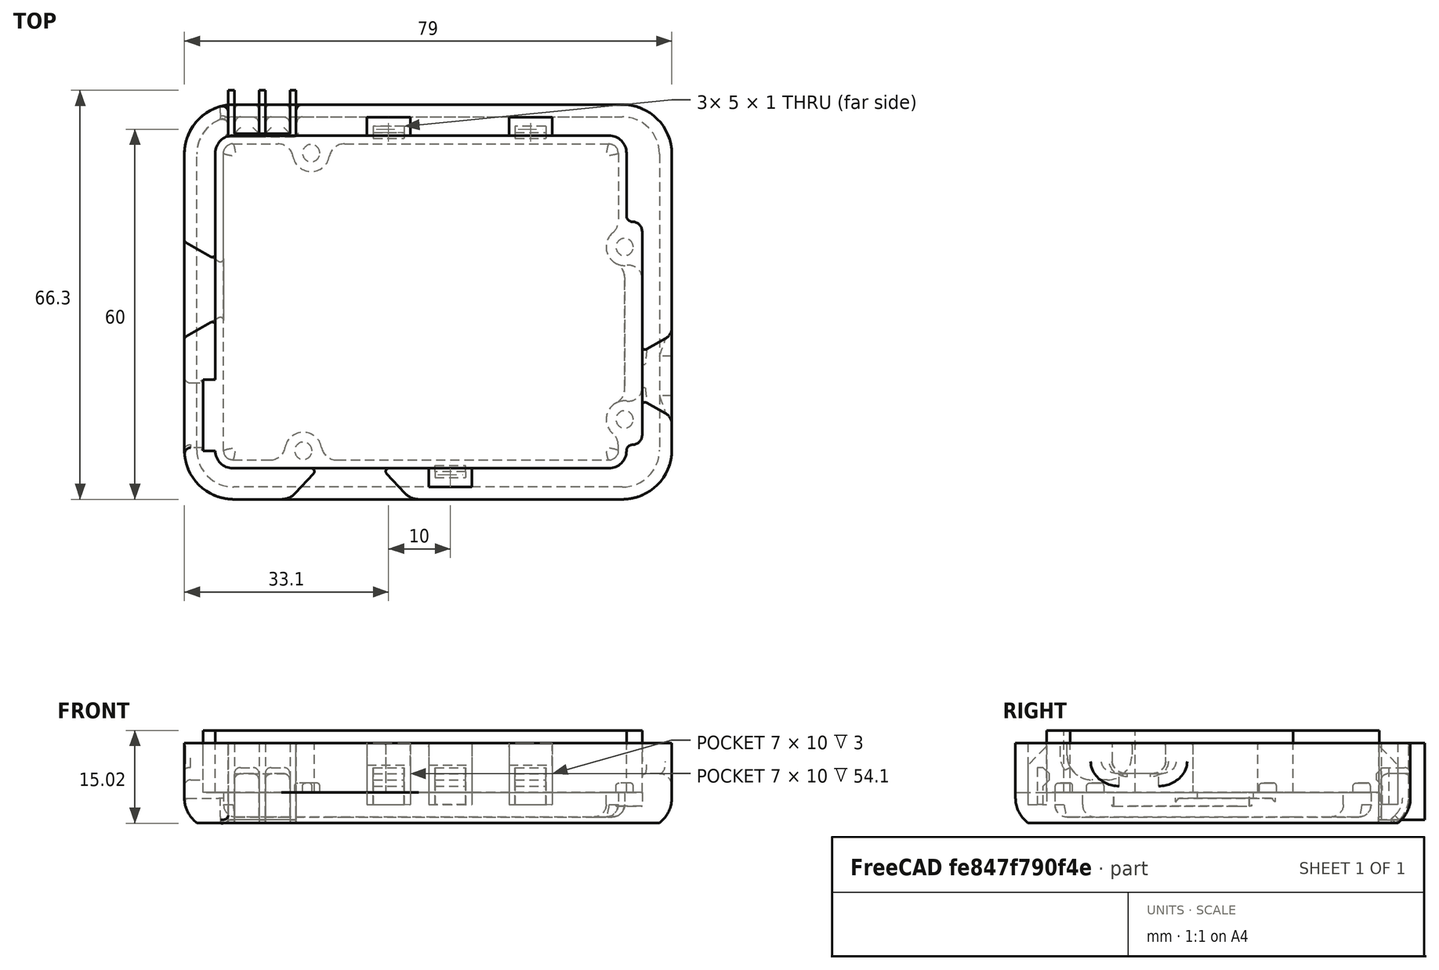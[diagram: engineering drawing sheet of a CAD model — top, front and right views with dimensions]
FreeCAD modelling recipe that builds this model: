
FCSTD DOCUMENT  (FreeCAD 0.16R6712 (Git))
Label: base_alhambra
License: All rights reserved
LicenseURL: http://en.wikipedia.org/wiki/All_rights_reserved
objects: PartDesign::Fillet×18, Sketcher::SketchObject×15, PartDesign::Pocket×9, PartDesign::Pad×6, Part::MultiFuse×5, Part::Cylinder×4, Part::Box×3, Part::Cut×1, PartDesign::Chamfer×1, Mesh::Feature×1, Part::Feature×1, Part::FeaturePython×1, Part::Mirroring×1
note: 80 computed .brp shape members not serialized (recipe doc carries the construction recipe); baked Part::Feature solids carry a one-line shape summary decoded from their .brp

FEATURE [Part::Cylinder] Cylinder  label="Cilindro"
  Angle = 360
  Height = 4.5
  Placement = pos=(-20.32,-24.13,0) rot=(0,0,1;0rad)
  Radius = 1.4
FEATURE [Part::Cylinder] Cylinder001  label="Cilindro001"
  Angle = 360
  Height = 4.5
  Placement = pos=(31.75,-19.05,0) rot=(0,0,1;0rad)
  Radius = 1.4
FEATURE [Part::Cylinder] Cylinder002  label="Cilindro002"
  Angle = 360
  Height = 4.5
  Placement = pos=(31.75,8.9,0) rot=(0,0,1;0rad)
  Radius = 1.4
FEATURE [Part::Cylinder] Cylinder003  label="Cilindro003"
  Angle = 360
  Height = 4.5
  Placement = pos=(-19.05,24.13,0) rot=(0,0,1;0rad)
  Radius = 1.4
FEATURE [Sketcher::SketchObject] Sketch
  Placement = pos=(0,0,3) rot=(0,0,1;0rad)
  sketch-geometry (16):
    g0: LineSegment StartX=-34.59 StartY=-24.13 StartZ=0 EndX=-36.59 EndY=-24.13 EndZ=0
    g1: LineSegment StartX=-36.59 StartY=-24.13 StartZ=0 EndX=-36.59 EndY=-12.63 EndZ=0
    g2: LineSegment StartX=-36.59 StartY=-12.63 StartZ=0 EndX=-34.59 EndY=-12.63 EndZ=0
    g3: LineSegment StartX=-34.59 StartY=-12.63 StartZ=0 EndX=-34.59 EndY=24.13 EndZ=0
    g4: ArcOfCircle CenterX=-31.75 CenterY=24.13 CenterZ=0 NormalX=0 NormalY=0 NormalZ=1 Radius=2.84 StartAngle=1.5708 EndAngle=3.14159
    g5: LineSegment StartX=-31.75 StartY=26.97 StartZ=0 EndX=29.21 EndY=26.97 EndZ=0
    g6: ArcOfCircle CenterX=29.21 CenterY=24.13 CenterZ=0 NormalX=0 NormalY=0 NormalZ=1 Radius=2.84 StartAngle=3.7035e-08 EndAngle=1.5708
    g7: LineSegment StartX=32.05 StartY=24.13 StartZ=0 EndX=32.05 EndY=13.97 EndZ=0
    g8: ArcOfCircle CenterX=33.02 CenterY=13.97 CenterZ=0 NormalX=0 NormalY=0 NormalZ=1 Radius=0.969997 StartAngle=3.14159 EndAngle=4.71239
    g9: ArcOfCircle CenterX=33.02 CenterY=11.43 CenterZ=0 NormalX=0 NormalY=0 NormalZ=1 Radius=1.57 StartAngle=6.28319 EndAngle=7.85398
    g10: LineSegment StartX=34.59 StartY=11.43 StartZ=0 EndX=34.59 EndY=-21.59 EndZ=0
    g11: ArcOfCircle CenterX=33.02 CenterY=-21.59 CenterZ=0 NormalX=0 NormalY=0 NormalZ=1 Radius=1.57 StartAngle=4.71239 EndAngle=6.28319
    g12: ArcOfCircle CenterX=33.02 CenterY=-24.13 CenterZ=0 NormalX=0 NormalY=0 NormalZ=1 Radius=0.97 StartAngle=1.5708 EndAngle=3.1416
    g13: ArcOfCircle CenterX=29.21 CenterY=-24.13 CenterZ=0 NormalX=0 NormalY=0 NormalZ=1 Radius=2.83999 StartAngle=4.71238 EndAngle=6.28319
    g14: LineSegment StartX=29.21 StartY=-26.97 StartZ=0 EndX=-31.75 EndY=-26.97 EndZ=0
    g15: ArcOfCircle CenterX=-31.75 CenterY=-24.13 CenterZ=0 NormalX=0 NormalY=0 NormalZ=1 Radius=2.84 StartAngle=3.14159 EndAngle=4.71239
  constraints (56):
    c: Horizontal(g0)
    c: Coincident(g0,g1)
    c: Vertical(g1)
    c: Coincident(g1,g2)
    c: Horizontal(g2)
    c: Coincident(g2,g3)
    c: Vertical(g3)
    c: Coincident(g4,g3)
    c: DistanceY(g2,g-1) = 12.63
    c: DistanceX(g2,g-1) = 34.59
    c: DistanceY(g-1,g3) = 24.13
    c: Tangent(g3,g4)
    c: DistanceY(g-1,g4) = 26.97
    c: DistanceX(g2,g2) = 2
    c: DistanceY(g1,g1) = 11.5
    c: DistanceX(g0,g0) = 2
    c: Coincident(g5,g4)
    c: Horizontal(g5)
    c: DistanceX(g5,g5) = 60.96
    c: Tangent(g4,g5)
    c: Coincident(g6,g5)
    c: Tangent(g6,g5)
    c: DistanceY(g-1,g6) = 24.13
    c: Coincident(g7,g6)
    c: Vertical(g7)
    c: DistanceY(g7,g7) = 10.16
    c: Tangent(g7,g6)
    c: Coincident(g8,g7)
    c: Coincident(g9,g8)
    c: Tangent(g8,g9)
    c: Tangent(g8,g7)
    c: Coincident(g10,g9)
    c: Vertical(g10)
    c: DistanceX(g-1,g10) = 34.59
    c: DistanceY(g10,g-1) = 21.59
    c: Tangent(g10,g9)
    c: DistanceY(g-1,g9) = 11.43
    c: Coincident(g11,g10)
    c: Coincident(g12,g11)
    c: Coincident(g13,g12)
    c: Tangent(g11,g12)
    c: Tangent(g11,g10)
    c: Tangent(g13,g12)
    c: DistanceX(g7,g8) = 0.97
    c: DistanceX(g11,g10) = 1.57
    c: DistanceX(g12,g11) = 0.97
    c: Radius(g11) = 1.57
    c: DistanceY(g13,g-1) = 26.97
    c: Coincident(g14,g13)
    c: Horizontal(g14)
    c: DistanceX(g14,g-1) = 31.75
    c: Coincident(g15,g14)
    c: Coincident(g15,g0)
    c: Radius(g15) = 2.84
    c: DistanceX(g-1,g13) = 29.21
    c: Tangent(g14,g13)
FEATURE [PartDesign::Pad] Pad  label="placa"
  Length = 10
  Length2 = 100
  Placement = pos=(0,0,3) rot=(0,0,1;0rad)
  Sketch = -> Sketch
  Type = 0
FEATURE [Sketcher::SketchObject] Sketch001
  ExternalGeometry = -> [Pad]
  Placement = pos=(0,0,3) rot=(1,0,0;3.14159rad)
  Support = -> Pad [Face17]
  sketch-geometry (24):
    g0: ArcOfCircle CenterX=29.21 CenterY=24.13 CenterZ=0 NormalX=0 NormalY=0 NormalZ=1 Radius=1.5 StartAngle=6.28318 EndAngle=7.85398
    g1: ArcOfCircle CenterX=31.77 CenterY=19.04 CenterZ=0 NormalX=0 NormalY=0 NormalZ=1 Radius=3 StartAngle=2.27479 EndAngle=4.23644
    g2: ArcOfCircle CenterX=-20.32 CenterY=24.13 CenterZ=0 NormalX=0 NormalY=0 NormalZ=1 Radius=3 StartAngle=3.32443 EndAngle=6.10035
    g3: ArcOfCircle CenterX=-14.9117 CenterY=23.13 CenterZ=0 NormalX=0 NormalY=0 NormalZ=1 Radius=2.5 StartAngle=1.5708 EndAngle=2.95876
    g4: LineSegment StartX=-14.9117 StartY=25.63 StartZ=0 EndX=29.21 EndY=25.63 EndZ=0
    g5: ArcOfCircle CenterX=-31.75 CenterY=24.13 CenterZ=0 NormalX=0 NormalY=0 NormalZ=1 Radius=1.50001 StartAngle=1.5708 EndAngle=3.14159
    g6: LineSegment StartX=-31.75 StartY=25.63 StartZ=0 EndX=-25.7283 EndY=25.63 EndZ=0
    g7: ArcOfCircle CenterX=-25.7283 CenterY=23.13 CenterZ=0 NormalX=0 NormalY=0 NormalZ=1 Radius=2.5 StartAngle=0.182833 EndAngle=1.5708
    g8: LineSegment StartX=-33.25 StartY=24.13 StartZ=0 EndX=-33.25 EndY=-24.13 EndZ=0
    g9: ArcOfCircle CenterX=-31.75 CenterY=-24.13 CenterZ=0 NormalX=0 NormalY=0 NormalZ=1 Radius=1.50001 StartAngle=3.14159 EndAngle=4.71239
    g10: ArcOfCircle CenterX=-19.05 CenterY=-24.13 CenterZ=0 NormalX=0 NormalY=0 NormalZ=1 Radius=3 StartAngle=0.182835 EndAngle=2.95876
    g11: ArcOfCircle CenterX=-24.4583 CenterY=-23.13 CenterZ=0 NormalX=0 NormalY=0 NormalZ=1 Radius=2.5 StartAngle=4.71239 EndAngle=6.10035
    g12: LineSegment StartX=-31.75 StartY=-25.63 StartZ=0 EndX=-24.4583 EndY=-25.63 EndZ=0
    g13: ArcOfCircle CenterX=-13.6417 CenterY=-23.13 CenterZ=0 NormalX=0 NormalY=0 NormalZ=1 Radius=2.5 StartAngle=3.32443 EndAngle=4.71239
    g14: LineSegment StartX=-13.6417 StartY=-25.63 StartZ=0 EndX=29.21 EndY=-25.63 EndZ=0
    g15: ArcOfCircle CenterX=29.21 CenterY=-24.13 CenterZ=0 NormalX=0 NormalY=0 NormalZ=1 Radius=1.5 StartAngle=4.71239 EndAngle=6.28319
    g16: ArcOfCircle CenterX=31.75 CenterY=-8.9 CenterZ=0 NormalX=0 NormalY=0 NormalZ=1 Radius=3 StartAngle=2.04266 EndAngle=4.01315
    g17: ArcOfCircle CenterX=28.21 CenterY=-13.1093 CenterZ=0 NormalX=0 NormalY=0 NormalZ=1 Radius=2.5 StartAngle=6.2812e-08 EndAngle=0.871554
    g18: LineSegment StartX=30.71 StartY=-24.13 StartZ=0 EndX=30.71 EndY=-13.1093 EndZ=0
    g19: ArcOfCircle CenterX=29.25 CenterY=-4.00102 CenterZ=0 NormalX=0 NormalY=0 NormalZ=1 Radius=2.5 StartAngle=5.18425 EndAngle=6.28319
    g20: ArcOfCircle CenterX=29.25 CenterY=14.1513 CenterZ=0 NormalX=0 NormalY=0 NormalZ=1 Radius=2.5 StartAngle=6.28319 EndAngle=7.37804
    g21: LineSegment StartX=31.75 StartY=14.1513 StartZ=0 EndX=31.75 EndY=-4.00102 EndZ=0
    g22: LineSegment StartX=30.71 StartY=24.13 StartZ=0 EndX=30.71 EndY=23.2324 EndZ=0
    g23: ArcOfCircle CenterX=28.21 CenterY=23.2324 CenterZ=0 NormalX=0 NormalY=0 NormalZ=1 Radius=2.5 StartAngle=5.41639 EndAngle=6.28318
  constraints (84):
    c: Coincident(g0,g-3)
    c: Radius(g1) = 3
    c: Radius(g0) = 1.5
    c: DistanceY(g1,g-4) = 2.55
    c: DistanceX(g1,g-4) = 2.82
    c: DistanceY(g-1,g2) = 24.13
    c: DistanceX(g2,g-1) = 20.32
    c: Radius(g2) = 3
    c: Coincident(g3,g2)
    c: Coincident(g4,g3)
    c: Coincident(g4,g0)
    c: Horizontal(g4)
    c: Tangent(g4,g0)
    c: Tangent(g3,g4)
    c: Tangent(g2,g3)
    c: Radius(g3) = 2.5
    c: Coincident(g5,g-6)
    c: PointOnObject(g5,g4)
    c: Tangent(g5,g4) = 1.5708
    c: Coincident(g6,g5)
    c: Horizontal(g6)
    c: Coincident(g7,g2)
    c: Coincident(g7,g6)
    c: Tangent(g7,g2)
    c: Tangent(g6,g7)
    c: Radius(g7) = 2.5
    c: Coincident(g8,g5)
    c: Vertical(g8)
    c: Coincident(g9,g-7)
    c: Coincident(g9,g8)
    c: Tangent(g9,g8)
    c: Tangent(g5,g8)
    c: DistanceY(g10,g-1) = 24.13
    c: DistanceX(g10,g-1) = 19.05
    c: Radius(g10) = 3
    c: Coincident(g11,g10)
    c: Coincident(g12,g9)
    c: Coincident(g12,g11)
    c: Horizontal(g12)
    c: Tangent(g9,g12)
    c: Tangent(g12,g11)
    c: Tangent(g11,g10)
    c: Radius(g11) = 2.5
    c: Coincident(g13,g10)
    c: Tangent(g13,g10)
    c: Coincident(g14,g13)
    c: Horizontal(g14)
    c: Coincident(g15,g-8)
    c: Coincident(g15,g14)
    c: Coincident(g17,g16)
    c: Tangent(g15,g14)
    c: Tangent(g14,g13)
    c: Radius(g15) = 1.5
    c: Radius(g13) = 2.5
    c: Coincident(g18,g15)
    c: Coincident(g18,g17)
    c: Vertical(g18)
    c: Tangent(g15,g18)
    c: DistanceX(g-1,g16) = 31.75
    c: DistanceY(g16,g-1) = 8.9
    c: Tangent(g16,g17)
    c: Tangent(g17,g18)
    c: Radius(g16) = 3
    c: Coincident(g19,g16)
    c: Coincident(g20,g1)
    c: Coincident(g21,g20)
    c: Coincident(g21,g19)
    c: Vertical(g21)
    c: Tangent(g19,g21)
    c: Tangent(g19,g16)
    c: Radius(g19) = 2.5
    c: Radius(g17) = 2.5
    c: Tangent(g20,g21)
    c: Tangent(g20,g1)
    c: Radius(g20) = 2.5
    c: DistanceX(g-1,g20) = 31.75
    c: Coincident(g22,g0)
    c: Vertical(g22)
    c: Tangent(g22,g0)
    c: Coincident(g23,g1)
    c: Coincident(g23,g22)
    c: Tangent(g23,g22)
    c: Tangent(g23,g1)
    c: Radius(g23) = 2.5
FEATURE [PartDesign::Pad] Pad001
  Length = 4
  Length2 = 100
  Placement = pos=(0,0,3) rot=(0,0,1;0rad)
  Sketch = -> Sketch001
  Type = 0
FEATURE [Part::Box] Box  label="Cubo"
  Height = 13
  Length = 79
  Placement = pos=(-39.6,-32,-2) rot=(0,0,1;0rad)
  Width = 64
FEATURE [PartDesign::Fillet] Fillet
  Base = -> Box [Edge7,Edge3,Edge5,Edge1]
  Placement = pos=(-39.6,-32,-2) rot=(0,0,1;0rad)
  Radius = 8
FEATURE [Part::Cut] Cut
  Base = -> Fillet
  Tool = -> Pad001
FEATURE [PartDesign::Chamfer] Chamfer
  Base = -> Cut [Edge4,Edge28,Edge30,Edge32,Edge33,Edge34,Edge35,Edge36]
  Size = 2
FEATURE [PartDesign::Fillet] Fillet001
  Base = -> Chamfer [Edge37,Edge5,Edge2,Edge33,Edge49,Edge51,Edge52,Edge46]
  Radius = 5
FEATURE [PartDesign::Fillet] Fillet002
  Base = -> Fillet001 [Edge155,Edge152,Edge151,Edge148,Edge147,Edge144,Edge143,Edge141,Edge139,Edge137,Edge135,Edge132,Edge130,Edge176,Edge175,Edge173,Edge171,Edge168,Edge167,Edge164,Edge163,Edge160,Edge159,Edge156]
  Radius = 2
FEATURE [PartDesign::Fillet] Fillet003
  Base = -> Fillet002 [Edge83,Edge76,Edge74,Edge79]
  Radius = 0.5
FEATURE [Part::MultiFuse] Fusion
  Shapes = -> [Cylinder003,Cylinder002,Cylinder001,Cylinder]
FEATURE [PartDesign::Fillet] Fillet004  label="tetones"
  Base = -> Fusion [Edge4,Edge10,Edge7,Edge1]
  Radius = 0.5
FEATURE [Mesh::Feature] Icezum_Alhambra_Support_with_text  label="Icezum-Alhambra-Support-with-text"
FEATURE [Part::Feature] Icezum_Alhambra_Support_with_text001
  shape: bbox 75.21 x 82 x 7 mm, 5620 faces, 0 solids (baked)
FEATURE [Sketcher::SketchObject] Sketch002
  Placement = pos=(0,0,11) rot=(0,0,1;0rad)
  Support = -> Fillet003 [Face46]
  sketch-geometry (4):
    g0: LineSegment StartX=-40 StartY=10 StartZ=0 EndX=-33 EndY=6 EndZ=0
    g1: LineSegment StartX=-33 StartY=6 StartZ=0 EndX=-33 EndY=-2 EndZ=0
    g2: LineSegment StartX=-33 StartY=-2 StartZ=0 EndX=-40 EndY=-6 EndZ=0
    g3: LineSegment StartX=-40 StartY=-6 StartZ=0 EndX=-40 EndY=10 EndZ=0
  constraints (12):
    c: Coincident(g0,g1)
    c: Coincident(g1,g2)
    c: Coincident(g2,g3)
    c: Coincident(g3,g0)
    c: Vertical(g1)
    c: Vertical(g3)
    c: DistanceY(g1,g-1) = 2
    c: DistanceY(g-1,g0) = 6
    c: DistanceY(g2,g1) = 4
    c: DistanceY(g0,g0) = 4
    c: DistanceX(g2,g1) = 7
    c: DistanceX(g1,g-1) = 33
FEATURE [PartDesign::Pocket] Pocket  label="usb"
  Length = 9
  Sketch = -> Sketch002
  Type = 0
FEATURE [PartDesign::Fillet] Fillet005
  Base = -> Pocket [Edge120,Edge71,Edge62,Edge68]
  Radius = 0.5
FEATURE [PartDesign::Fillet] Fillet006
  Base = -> Fillet005 [Edge151,Edge178,Edge63]
  Radius = 0.5
FEATURE [Sketcher::SketchObject] Sketch003
  Placement = pos=(0,0,11) rot=(0,0,1;0rad)
  Support = -> Fillet006 [Face2]
  sketch-geometry (4):
    g0: LineSegment StartX=-23 StartY=-32.5 StartZ=0 EndX=-17 EndY=-26 EndZ=0
    g1: LineSegment StartX=-17 StartY=-26 StartZ=0 EndX=-8.5 EndY=-26 EndZ=0
    g2: LineSegment StartX=-8.5 StartY=-26 StartZ=0 EndX=-2.5 EndY=-32.5 EndZ=0
    g3: LineSegment StartX=-2.5 StartY=-32.5 StartZ=0 EndX=-23 EndY=-32.5 EndZ=0
  constraints (12):
    c: Coincident(g0,g1)
    c: Horizontal(g1)
    c: Coincident(g1,g2)
    c: Coincident(g2,g3)
    c: Horizontal(g3)
    c: Coincident(g3,g0)
    c: DistanceX(g0,g-1) = 17
    c: DistanceY(g0,g-1) = 26
    c: DistanceY(g0,g0) = 6.5
    c: DistanceX(g1,g1) = 8.5
    c: DistanceX(g1,g2) = 6
    c: DistanceX(g0,g0) = 6
FEATURE [PartDesign::Pocket] Pocket001
  Length = 8
  Sketch = -> Sketch003
  Type = 0
FEATURE [PartDesign::Fillet] Fillet007
  Base = -> Pocket001 [Edge46,Edge44]
  Radius = 3
FEATURE [PartDesign::Fillet] Fillet008
  Base = -> Fillet007 [Edge32,Edge154]
  Radius = 0.5
FEATURE [Sketcher::SketchObject] Sketch004
  Placement = pos=(0,0,11) rot=(0,0,1;0rad)
  Support = -> Fillet008 [Face22]
  sketch-geometry (4):
    g0: LineSegment StartX=33 StartY=-9 StartZ=0 EndX=40 EndY=-5 EndZ=0
    g1: LineSegment StartX=40 StartY=-5 StartZ=0 EndX=40 EndY=-19 EndZ=0
    g2: LineSegment StartX=40 StartY=-19 StartZ=0 EndX=33 EndY=-15 EndZ=0
    g3: LineSegment StartX=33 StartY=-15 StartZ=0 EndX=33 EndY=-9 EndZ=0
  constraints (12):
    c: Coincident(g0,g1)
    c: Vertical(g1)
    c: Coincident(g1,g2)
    c: Coincident(g2,g3)
    c: Coincident(g3,g0)
    c: Vertical(g3)
    c: DistanceY(g3,g3) = 6
    c: DistanceX(g-1,g2) = 33
    c: DistanceY(g0,g-1) = 9
    c: DistanceY(g0,g0) = 4
    c: DistanceY(g1,g2) = 4
    c: DistanceX(g2,g1) = 7
FEATURE [PartDesign::Pocket] Pocket002
  Length = 5
  Sketch = -> Sketch004
  Type = 0
FEATURE [PartDesign::Fillet] Fillet009
  Base = -> Pocket002 [Edge228,Edge229,Edge227,Edge249,Edge226]
  Radius = 2
FEATURE [PartDesign::Fillet] Fillet010
  Base = -> Fillet009 [Edge20,Edge22,Edge24,Edge15,Edge19]
  Radius = 0.5
FEATURE [Sketcher::SketchObject] Sketch005
  Placement = pos=(0,0,11) rot=(0,0,1;0rad)
  Support = -> Fillet010 [Face23]
  sketch-geometry (12):
    g0: LineSegment StartX=-31.5 StartY=27.3 StartZ=0 EndX=-27.5 EndY=27.3 EndZ=0
    g1: LineSegment StartX=-27.5 StartY=27.3 StartZ=0 EndX=-27.5 EndY=34.3 EndZ=0
    g2: LineSegment StartX=-27.5 StartY=34.3 StartZ=0 EndX=-26.5 EndY=34.3 EndZ=0
    g3: LineSegment StartX=-26.5 StartY=34.3 StartZ=0 EndX=-26.5 EndY=27.3 EndZ=0
    g4: LineSegment StartX=-26.5 StartY=27.3 StartZ=0 EndX=-22.5 EndY=27.3 EndZ=0
    g5: LineSegment StartX=-22.5 StartY=27.3 StartZ=0 EndX=-22.5 EndY=34.3 EndZ=0
    g6: LineSegment StartX=-22.5 StartY=34.3 StartZ=0 EndX=-21.5 EndY=34.3 EndZ=0
    g7: LineSegment StartX=-21.5 StartY=34.3 StartZ=0 EndX=-21.5 EndY=26.8 EndZ=0
    g8: LineSegment StartX=-21.5 StartY=26.8 StartZ=0 EndX=-32.5 EndY=26.8 EndZ=0
    g9: LineSegment StartX=-32.5 StartY=26.8 StartZ=0 EndX=-32.5 EndY=34.3 EndZ=0
    g10: LineSegment StartX=-32.5 StartY=34.3 StartZ=0 EndX=-31.5 EndY=34.3 EndZ=0
    g11: LineSegment StartX=-31.5 StartY=34.3 StartZ=0 EndX=-31.5 EndY=27.3 EndZ=0
  constraints (36):
    c: Horizontal(g0)
    c: Coincident(g0,g1)
    c: Vertical(g1)
    c: Coincident(g1,g2)
    c: Horizontal(g2)
    c: Coincident(g2,g3)
    c: Vertical(g3)
    c: Coincident(g3,g4)
    c: Horizontal(g4)
    c: Coincident(g4,g5)
    c: Vertical(g5)
    c: Coincident(g5,g6)
    c: Horizontal(g6)
    c: Coincident(g6,g7)
    c: Vertical(g7)
    c: Coincident(g7,g8)
    c: Horizontal(g8)
    c: Coincident(g8,g9)
    c: Vertical(g9)
    c: Coincident(g9,g10)
    c: Horizontal(g10)
    c: Coincident(g10,g11)
    c: Coincident(g11,g0)
    c: Vertical(g11)
    c: Equal(g6,g2)
    c: Equal(g2,g10)
    c: Equal(g3,g11)
    c: Equal(g11,g5)
    c: Equal(g9,g7)
    c: DistanceX(g2,g2) = 1
    c: Equal(g4,g0)
    c: DistanceX(g0,g0) = 4
    c: DistanceY(g5,g5) = 7
    c: DistanceY(g7,g7) = 7.5
    c: DistanceX(g7,g-1) = 21.5
    c: DistanceY(g-1,g7) = 26.8
FEATURE [PartDesign::Pocket] Pocket003
  Length = 12.5
  Sketch = -> Sketch005
  Type = 0
FEATURE [Sketcher::SketchObject] Sketch006
  ExternalGeometry = -> [Pocket003]
  Placement = pos=(0,0,11) rot=(0,0,1;0rad)
  Support = -> Pocket003 [Face148]
  sketch-geometry (4):
    g0: LineSegment StartX=-31.5 StartY=32 StartZ=0 EndX=-22.5 EndY=32 EndZ=0
    g1: LineSegment StartX=-22.5 StartY=32 StartZ=0 EndX=-22.5 EndY=27.3 EndZ=0
    g2: LineSegment StartX=-22.5 StartY=27.3 StartZ=0 EndX=-31.5 EndY=27.3 EndZ=0
    g3: LineSegment StartX=-31.5 StartY=27.3 StartZ=0 EndX=-31.5 EndY=32 EndZ=0
  constraints (10):
    c: Coincident(g0,g1)
    c: Coincident(g1,g2)
    c: Coincident(g2,g3)
    c: Coincident(g3,g0)
    c: Horizontal(g0)
    c: Horizontal(g2)
    c: Vertical(g1)
    c: Vertical(g3)
    c: Coincident(g0,g-4)
    c: Coincident(g1,g-3)
FEATURE [PartDesign::Pocket] Pocket004
  Length = 5
  Sketch = -> Sketch006
  Type = 0
FEATURE [Sketcher::SketchObject] Sketch007
  ExternalGeometry = -> [Pocket004]
  Placement = pos=(0,0,-1.5) rot=(0,0,1;0rad)
  Support = -> Pocket004 [Face97]
  sketch-geometry (12):
    g0: LineSegment StartX=-31.5 StartY=32 StartZ=0 EndX=-32.5 EndY=32 EndZ=0
    g1: LineSegment StartX=-32.5 StartY=32 StartZ=0 EndX=-32.5 EndY=26.8 EndZ=0
    g2: LineSegment StartX=-32.5 StartY=26.8 StartZ=0 EndX=-31.5 EndY=26.8 EndZ=0
    g3: LineSegment StartX=-31.5 StartY=26.8 StartZ=0 EndX=-31.5 EndY=32 EndZ=0
    g4: LineSegment StartX=-27.5 StartY=32 StartZ=0 EndX=-26.5 EndY=32 EndZ=0
    g5: LineSegment StartX=-26.5 StartY=32 StartZ=0 EndX=-26.5 EndY=26.8 EndZ=0
    g6: LineSegment StartX=-26.5 StartY=26.8 StartZ=0 EndX=-27.5 EndY=26.8 EndZ=0
    g7: LineSegment StartX=-27.5 StartY=26.8 StartZ=0 EndX=-27.5 EndY=32 EndZ=0
    g8: LineSegment StartX=-21.5 StartY=26.8 StartZ=0 EndX=-22.5 EndY=26.8 EndZ=0
    g9: LineSegment StartX=-22.5 StartY=26.8 StartZ=0 EndX=-22.5 EndY=32 EndZ=0
    g10: LineSegment StartX=-22.5 StartY=32 StartZ=0 EndX=-21.5 EndY=32 EndZ=0
    g11: LineSegment StartX=-21.5 StartY=32 StartZ=0 EndX=-21.5 EndY=26.8 EndZ=0
  constraints (31):
    c: Coincident(g0,g1)
    c: Coincident(g1,g2)
    c: Coincident(g2,g3)
    c: Coincident(g3,g0)
    c: Horizontal(g0)
    c: Horizontal(g2)
    c: Vertical(g1)
    c: Vertical(g3)
    c: Coincident(g0,g-4)
    c: Coincident(g1,g-9)
    c: Coincident(g4,g5)
    c: Coincident(g5,g6)
    c: Coincident(g6,g7)
    c: Coincident(g7,g4)
    c: Horizontal(g4)
    c: Horizontal(g6)
    c: Vertical(g5)
    c: Vertical(g7)
    c: Coincident(g4,g-5)
    c: PointOnObject(g5,g-9)
    c: Coincident(g8,g9)
    c: Coincident(g9,g10)
    c: Coincident(g10,g11)
    c: Coincident(g11,g8)
    c: Horizontal(g8)
    c: Horizontal(g10)
    c: Vertical(g9)
    c: Vertical(g11)
    c: Coincident(g8,g-9)
    c: Coincident(g9,g-7)
    c: Coincident(g4,g-6)
FEATURE [PartDesign::Pocket] Pocket005
  Length = 5
  Sketch = -> Sketch007
  Type = 1
FEATURE [PartDesign::Fillet] Fillet011
  Base = -> Pocket005 [Edge382,Edge394,Edge380,Edge392,Edge261,Edge277,Edge378,Edge379,Edge375,Edge376,Edge288,Edge286]
  Radius = 1
FEATURE [PartDesign::Fillet] Fillet012
  Base = -> Fillet011 [Edge430,Edge431,Edge427,Edge309,Edge306,Edge429,Edge440,Edge441,Edge437,Edge322,Edge319,Edge439]
  Radius = 1
FEATURE [Sketcher::SketchObject] Sketch008
  ExternalGeometry = -> [Fillet012]
  Placement = pos=(0,0,11) rot=(0,0,1;0rad)
  Support = -> Fillet012 [Face145]
  sketch-geometry (12):
    g0: LineSegment StartX=-10 StartY=26.97 StartZ=0 EndX=-3 EndY=26.97 EndZ=0
    g1: LineSegment StartX=-3 StartY=26.97 StartZ=0 EndX=-3 EndY=29.97 EndZ=0
    g2: LineSegment StartX=-3 StartY=29.97 StartZ=0 EndX=-10 EndY=29.97 EndZ=0
    g3: LineSegment StartX=-10 StartY=29.97 StartZ=0 EndX=-10 EndY=26.97 EndZ=0
    g4: LineSegment StartX=13 StartY=26.97 StartZ=0 EndX=20 EndY=26.97 EndZ=0
    g5: LineSegment StartX=20 StartY=26.97 StartZ=0 EndX=20 EndY=29.97 EndZ=0
    g6: LineSegment StartX=20 StartY=29.97 StartZ=0 EndX=13 EndY=29.97 EndZ=0
    g7: LineSegment StartX=13 StartY=29.97 StartZ=0 EndX=13 EndY=26.97 EndZ=0
    g8: LineSegment StartX=0 StartY=-26.97 StartZ=0 EndX=7 EndY=-26.97 EndZ=0
    g9: LineSegment StartX=7 StartY=-26.97 StartZ=0 EndX=7 EndY=-29.97 EndZ=0
    g10: LineSegment StartX=7 StartY=-29.97 StartZ=0 EndX=0 EndY=-29.97 EndZ=0
    g11: LineSegment StartX=0 StartY=-29.97 StartZ=0 EndX=0 EndY=-26.97 EndZ=0
  constraints (36):
    c: Coincident(g0,g1)
    c: Coincident(g1,g2)
    c: Coincident(g2,g3)
    c: Coincident(g3,g0)
    c: Horizontal(g0)
    c: Horizontal(g2)
    c: Vertical(g1)
    c: Vertical(g3)
    c: PointOnObject(g0,g-3)
    c: Coincident(g4,g5)
    c: Coincident(g5,g6)
    c: Coincident(g6,g7)
    c: Coincident(g7,g4)
    c: Horizontal(g4)
    c: Horizontal(g6)
    c: Vertical(g5)
    c: Vertical(g7)
    c: PointOnObject(g4,g-3)
    c: Coincident(g8,g9)
    c: Coincident(g9,g10)
    c: Coincident(g10,g11)
    c: Coincident(g11,g8)
    c: Horizontal(g8)
    c: Horizontal(g10)
    c: Vertical(g9)
    c: Vertical(g11)
    c: PointOnObject(g8,g-4)
    c: Equal(g2,g6)
    c: Equal(g6,g10)
    c: DistanceX(g10,g10) = 7
    c: Equal(g1,g7)
    c: Equal(g7,g11)
    c: DistanceY(g9,g9) = 3
    c: DistanceX(g0,g-1) = 3
    c: DistanceX(g0,g4) = 23
    c: PointOnObject(g8,g-2)
FEATURE [PartDesign::Pocket] Pocket006
  Length = 10
  Sketch = -> Sketch008
  Type = 0
FEATURE [Sketcher::SketchObject] Sketch009
  Placement = pos=(-9,0,0) rot=(0.57735,0.57735,0.57735;2.0944rad)
  sketch-geometry (7):
    g0: LineSegment StartX=27.5 StartY=-1 StartZ=0 EndX=27.5 EndY=4 EndZ=0
    g1: LineSegment StartX=27.5 StartY=4 StartZ=0 EndX=26.5 EndY=5 EndZ=0
    g2: LineSegment StartX=26.5 StartY=5 StartZ=0 EndX=26.5 EndY=6 EndZ=0
    g3: LineSegment StartX=26.5 StartY=6 StartZ=0 EndX=27.5 EndY=7 EndZ=0
    g4: LineSegment StartX=27.5 StartY=7 StartZ=0 EndX=28.5 EndY=7 EndZ=0
    g5: LineSegment StartX=28.5 StartY=7 StartZ=0 EndX=28.5 EndY=-1 EndZ=0
    g6: LineSegment StartX=28.5 StartY=-1 StartZ=0 EndX=27.5 EndY=-1 EndZ=0
  constraints (21):
    c: Vertical(g0)
    c: Coincident(g0,g1)
    c: Coincident(g1,g2)
    c: Vertical(g2)
    c: Coincident(g2,g3)
    c: Coincident(g3,g4)
    c: Coincident(g4,g5)
    c: Vertical(g5)
    c: Coincident(g5,g6)
    c: Coincident(g6,g0)
    c: Horizontal(g6)
    c: DistanceX(g1,g0) = 1
    c: DistanceY(g0,g0) = 5
    c: Angle(g1,g2) = 2.35619
    c: Perpendicular(g1,g3)
    c: DistanceY(g2,g2) = 1
    c: Horizontal(g4)
    c: DistanceX(g6,g6) = 1
    c: Equal(g3,g1)
    c: DistanceX(g-1,g0) = 27.5
    c: DistanceY(g0,g-1) = 1
FEATURE [PartDesign::Pad] Pad002
  Length = 5
  Length2 = 100
  Placement = pos=(-9,0,0) rot=(0.57735,0.57735,0.57735;2.0944rad)
  Sketch = -> Sketch009
  Type = 0
FEATURE [Part::FeaturePython] Clone  label="Clone of Pad002"  # Draft clone (typed FeaturePython)
  Objects = -> [Pad002]
  Placement = pos=(14,0,0) rot=(0.57735,0.57735,0.57735;2.0944rad)
  Scale = (1,1,1)
FEATURE [Part::Mirroring] Part__Mirroring  label="Clone of Pad002 (Mirror #1)"
  Base = (0,0,0)
  Normal = (0,1,0)
  Placement = pos=(-13,0,0) rot=(0,0,1;0rad)
  Source = -> Clone
FEATURE [Part::MultiFuse] Fusion001  label="lenguetas"
  Shapes = -> [Part__Mirroring,Pad002,Clone]
FEATURE [Part::MultiFuse] Fusion002
  Shapes = -> [Fusion001,Pocket006]
FEATURE [Sketcher::SketchObject] Sketch010
  ExternalGeometry = -> [Fusion002]
  Placement = pos=(0,0,11) rot=(0,0,1;0rad)
  Support = -> Fusion002 [Face156]
  sketch-geometry (4):
    g0: LineSegment StartX=-41.09 StartY=-13.13 StartZ=0 EndX=-35.09 EndY=-13.13 EndZ=0
    g1: LineSegment StartX=-35.09 StartY=-13.13 StartZ=0 EndX=-35.09 EndY=-23.63 EndZ=0
    g2: LineSegment StartX=-35.09 StartY=-23.63 StartZ=0 EndX=-41.09 EndY=-23.63 EndZ=0
    g3: LineSegment StartX=-41.09 StartY=-23.63 StartZ=0 EndX=-41.09 EndY=-13.13 EndZ=0
  constraints (12):
    c: Coincident(g0,g1)
    c: Coincident(g1,g2)
    c: Coincident(g2,g3)
    c: Coincident(g3,g0)
    c: Horizontal(g0)
    c: Horizontal(g2)
    c: Vertical(g1)
    c: Vertical(g3)
    c: DistanceY(g-4,g1) = 0.5
    c: DistanceY(g0,g-3) = 0.5
    c: PointOnObject(g-3,g1)
    c: DistanceX(g0,g0) = 6
FEATURE [PartDesign::Pocket] Pocket007
  Length = 6
  Sketch = -> Sketch010
  Type = 0
FEATURE [PartDesign::Fillet] Fillet013
  Base = -> Pocket007 [Edge464,Edge461]
  Radius = 4
FEATURE [PartDesign::Fillet] Fillet014
  Base = -> Fillet013 [Edge99,Edge97,Edge95,Edge94,Edge7]
  Radius = 1
FEATURE [PartDesign::Fillet] Fillet015
  Base = -> Fillet014 [Edge214,Edge248,Edge252,Edge204,Edge194,Edge191,Edge186,Edge167,Edge179,Edge176,Edge161,Edge158,Edge153,Edge150,Edge145,Edge139,Edge24,Edge156,Edge17,Edge11,Edge18,Edge4,Edge19,Edge13,Edge20,Edge21,Edge22,Edge23,Edge25]
  Radius = 0.4
FEATURE [Part::MultiFuse] Fusion003
  Shapes = -> [Fillet004,Fillet015]
FEATURE [Sketcher::SketchObject] Sketch011
  ExternalGeometry = -> [Fusion003]
  Placement = pos=(-10,0,0) rot=(0.57735,0.57735,0.57735;2.0944rad)
  Support = -> Fusion003 [Face139]
  sketch-geometry (4):
    g0: ArcOfCircle CenterX=27.37 CenterY=10.6 CenterZ=0 NormalX=0 NormalY=0 NormalZ=1 Radius=0.4 StartAngle=1.5708 EndAngle=3.92701
    g1: LineSegment StartX=27.0872 StartY=10.3172 StartZ=0 EndX=30.97 EndY=6.43431 EndZ=0
    g2: LineSegment StartX=30.97 StartY=6.43431 StartZ=0 EndX=30.97 EndY=11 EndZ=0
    g3: LineSegment StartX=27.37 StartY=11 StartZ=0 EndX=30.97 EndY=11 EndZ=0
  constraints (11):
    c: Coincident(g0,g-4)
    c: Coincident(g0,g-4)
    c: Coincident(g1,g0)
    c: Coincident(g2,g1)
    c: Vertical(g2)
    c: Coincident(g3,g0)
    c: Coincident(g3,g2)
    c: Horizontal(g3)
    c: DistanceX(g-3,g2) = 1
    c: Angle(g2,g1) = 0.785398
    c: Tangent(g1,g0)
FEATURE [PartDesign::Pad] Pad003
  Length = 31
  Length2 = 100
  Sketch = -> Sketch011
  Type = 0
FEATURE [Sketcher::SketchObject] Sketch012
  ExternalGeometry = -> [Pad003]
  Placement = pos=(0,0,0) rot=(0.57735,0.57735,0.57735;2.0944rad)
  Support = -> Pad003 [Face94]
  sketch-geometry (4):
    g0: ArcOfCircle CenterX=-27.37 CenterY=10.6 CenterZ=0 NormalX=0 NormalY=0 NormalZ=1 Radius=0.4 StartAngle=5.49781 EndAngle=7.85398
    g1: LineSegment StartX=-27.0872 StartY=10.3172 StartZ=0 EndX=-29.97 EndY=7.43431 EndZ=0
    g2: LineSegment StartX=-27.37 StartY=11 StartZ=0 EndX=-29.97 EndY=11 EndZ=0
    g3: LineSegment StartX=-29.97 StartY=11 StartZ=0 EndX=-29.97 EndY=7.43431 EndZ=0
  constraints (10):
    c: Coincident(g0,g-4)
    c: Coincident(g0,g-4)
    c: Coincident(g1,g0)
    c: Coincident(g2,g0)
    c: Coincident(g2,g-3)
    c: Coincident(g3,g2)
    c: Coincident(g3,g1)
    c: Tangent(g1,g0)
    c: Angle(g1,g3) = 0.785398
    c: Vertical(g3)
FEATURE [PartDesign::Pad] Pad004
  Length = 10
  Length2 = 100
  Sketch = -> Sketch012
  Type = 0
FEATURE [Sketcher::SketchObject] Sketch013
  ExternalGeometry = -> [Pad004]
  Placement = pos=(0,0,3) rot=(0,0,1;0rad)
  Support = -> Pad004 [Face4]
  sketch-geometry (6):
    g0: ArcOfCircle CenterX=31.77 CenterY=-19.04 CenterZ=0 NormalX=0 NormalY=0 NormalZ=1 Radius=3 StartAngle=1.44865 EndAngle=2.04675
    g1: ArcOfCircle CenterX=32.4021 CenterY=-13.8908 CenterZ=0 NormalX=0 NormalY=0 NormalZ=1 Radius=2.18787 StartAngle=4.59024 EndAngle=6.28319
    g2: LineSegment StartX=34.59 StartY=-13.8908 StartZ=0 EndX=34.59 EndY=3.75328 EndZ=0
    g3: ArcOfCircle CenterX=31.75 CenterY=8.9 CenterZ=0 NormalX=0 NormalY=0 NormalZ=1 Radius=3 StartAngle=4.24053 EndAngle=4.83843
    g4: ArcOfCircle CenterX=32.4021 CenterY=3.75328 CenterZ=0 NormalX=0 NormalY=0 NormalZ=1 Radius=2.18787 StartAngle=7.32987e-07 EndAngle=1.69683
    g5: LineSegment StartX=30.3864 StartY=6.22783 StartZ=0 EndX=30.3955 EndY=-16.3734 EndZ=0
  constraints (17):
    c: Coincident(g0,g-4)
    c: Coincident(g0,g-4)
    c: Coincident(g1,g0)
    c: Coincident(g1,g-5)
    c: Tangent(g0,g1)
    c: Tangent(g1,g-5) = 1.5708
    c: Coincident(g2,g1)
    c: Vertical(g2)
    c: Coincident(g3,g-3)
    c: Coincident(g3,g-3)
    c: Coincident(g4,g3)
    c: Coincident(g4,g2)
    c: Tangent(g4,g3)
    c: Tangent(g4,g2)
    c: Equal(g4,g1)
    c: Coincident(g5,g3)
    c: Coincident(g5,g0)
FEATURE [PartDesign::Pocket] Pocket008
  Length = 2.25
  Sketch = -> Sketch013
  Type = 0
FEATURE [Part::Box] Box001  label="Cubo001"
  Height = 2
  Length = 4
  Placement = pos=(-31.5,27.3,5) rot=(0,0,1;0rad)
  Width = 4.7
FEATURE [Part::Box] Box002  label="Cubo002"
  Height = 2
  Length = 4
  Placement = pos=(-26.5,27.3,5) rot=(0,0,1;0rad)
  Width = 4.7
FEATURE [PartDesign::Fillet] Fillet016
  Base = -> Box001 [Edge7,Edge3,Edge12,Edge2,Edge6]
  Placement = pos=(-31.5,27.3,5) rot=(0,0,1;0rad)
  Radius = 1
FEATURE [PartDesign::Fillet] Fillet017
  Base = -> Box002 [Edge3,Edge7,Edge12,Edge2,Edge6]
  Placement = pos=(-26.5,27.3,5) rot=(0,0,1;0rad)
  Radius = 1
FEATURE [Part::MultiFuse] Fusion004
  Shapes = -> [Pocket008,Fillet016,Fillet017]
FEATURE [Sketcher::SketchObject] Sketch014
  ExternalGeometry = -> [Fusion004]
  Placement = pos=(0,0,-1.5) rot=(0,0,1;0rad)
  Support = -> Fusion004 [Face229]
  sketch-geometry (8):
    g0: LineSegment StartX=-31.5 StartY=26.8 StartZ=0 EndX=-27.5 EndY=26.8 EndZ=0
    g1: LineSegment StartX=-27.5 StartY=26.8 StartZ=0 EndX=-27.5 EndY=27.3 EndZ=0
    g2: LineSegment StartX=-27.5 StartY=27.3 StartZ=0 EndX=-31.5 EndY=27.3 EndZ=0
    g3: LineSegment StartX=-31.5 StartY=27.3 StartZ=0 EndX=-31.5 EndY=26.8 EndZ=0
    g4: LineSegment StartX=-26.5 StartY=27.3 StartZ=0 EndX=-22.5 EndY=27.3 EndZ=0
    g5: LineSegment StartX=-22.5 StartY=27.3 StartZ=0 EndX=-22.5 EndY=26.8 EndZ=0
    g6: LineSegment StartX=-22.5 StartY=26.8 StartZ=0 EndX=-26.5 EndY=26.8 EndZ=0
    g7: LineSegment StartX=-26.5 StartY=26.8 StartZ=0 EndX=-26.5 EndY=27.3 EndZ=0
  constraints (20):
    c: Coincident(g0,g1)
    c: Coincident(g1,g2)
    c: Coincident(g2,g3)
    c: Coincident(g3,g0)
    c: Horizontal(g0)
    c: Horizontal(g2)
    c: Vertical(g1)
    c: Vertical(g3)
    c: Coincident(g0,g-3)
    c: Coincident(g1,g-4)
    c: Coincident(g4,g5)
    c: Coincident(g5,g6)
    c: Coincident(g6,g7)
    c: Coincident(g7,g4)
    c: Horizontal(g4)
    c: Horizontal(g6)
    c: Vertical(g5)
    c: Vertical(g7)
    c: Coincident(g4,g-5)
    c: Coincident(g5,g-6)
FEATURE [PartDesign::Pad] Pad005
  Length = 0.5
  Length2 = 100
  Sketch = -> Sketch014
  Type = 0
